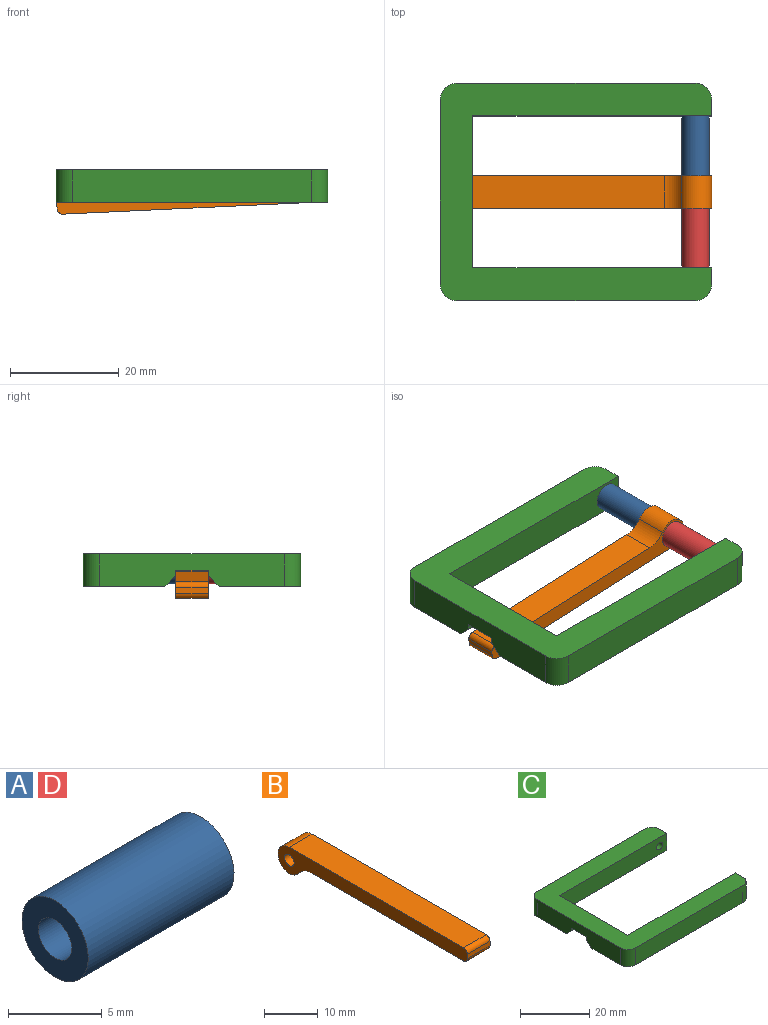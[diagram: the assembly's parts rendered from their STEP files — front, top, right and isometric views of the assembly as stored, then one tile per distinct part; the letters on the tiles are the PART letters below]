
ASSEMBLY  parts=4 mates=4
PART A: 4 faces, bbox 11x5x5 mm
  f0: cylinder r=1.25mm len=11mm, axis (-1,0,0), area 86.4mm2, adj f2,f3
  f1: cylinder r=2.5mm len=11mm, axis (-1,0,0), area 172.8mm2, adj f2,f3
  f2: plane 5x5mm, normal (1,0,0), area 14.7mm2, adj f0,f1
  f3: plane 5x5mm, normal (-1,0,0), area 14.7mm2, adj f0,f1
PART B: 10 faces, bbox 6x50x6 mm
  f0: plane 46x6mm, normal (0,0,1), area 276mm2, adj f4,f6,f7,f8
  f1: plane 6x1mm, normal (0,-1,0), area 6mm2, adj f6,f7,f8,f9
  f2: plane 40.26x6mm, normal (0,0,-1), area 241.5mm2, adj f3,f6,f7,f9
  f3: cylinder r=4mm len=6mm, axis (-1,0,0), area 23.1mm2, adj f2,f4,f6,f7
  f4: cylinder r=3mm len=6mm, axis (-1,0,0), area 73.9mm2, adj f0,f3,f6,f7
  f5: cylinder r=1.25mm len=6mm, axis (-1,0,0), area 47.1mm2, adj f6,f7
  f6: plane 50x6mm, normal (1,0,0), area 157.9mm2, adj f0,f1,f2,f3,f4,f5,f8,f9
  f7: plane 50x6mm, normal (-1,0,0), area 157.9mm2, adj f0,f1,f2,f3,f4,f5,f8,f9
  f8: cylinder r=1mm len=6mm, axis (1,0,0), area 9.4mm2, adj f0,f1,f6,f7
  f9: cylinder r=1mm len=6mm, axis (-1,0,0), area 9.4mm2, adj f1,f2,f6,f7
PART C: 66 faces, bbox 50x40x6 mm
  f0: plane 50x15mm, normal (0,0,-1), area 342.5mm2, adj f1,f2,f3,f4,f5,f6,f12,f21
  f1: plane 28x6mm, normal (1,0,0), area 146mm2, adj f0,f11,f12,f13,f14,f18,f19,f20
  f2: plane 44x6mm, normal (0,1,0), area 261.5mm2, adj f0,f4,f5,f13,f15
  f3: plane 6x3mm, normal (1,0,0), area 18mm2, adj f0,f4,f12,f13
  f4: cylinder r=3mm len=6mm, axis (0,0,-1), area 25.8mm2, adj f0,f2,f3,f13,f15
  f5: cylinder r=3mm len=6mm, axis (0,0,-1), area 28.3mm2, adj f0,f2,f6,f13
  f6: plane 34x6mm, normal (-1,0,0), area 182mm2, adj f0,f5,f7,f13,f14,f18,f19,f20
  f7: cylinder r=3mm len=6mm, axis (0,0,-1), area 28.3mm2, adj f6,f8,f13,f14
  f8: plane 44x6mm, normal (0,-1,0), area 264mm2, adj f7,f9,f13,f14
  f9: cylinder r=3mm len=6mm, axis (0,0,-1), area 28.3mm2, adj f8,f10,f13,f14
  f10: plane 6x3mm, normal (1,0,0), area 18mm2, adj f9,f11,f13,f14
  f11: plane 44x6mm, normal (0,1,0), area 259.1mm2, adj f1,f10,f13,f14,f16
  f12: plane 44x6mm, normal (0,-1,0), area 259.1mm2, adj f0,f1,f3,f13,f15
  f13: plane 50x40mm, normal (0,0,1), area 760.3mm2, adj f1,f2,f3,f4,f5,f6,f7,f8
  f14: plane 50x15mm, normal (0,0,-1), area 350.1mm2, adj f1,f6,f7,f8,f9,f10,f11,f22
  f15: cylinder r=1.25mm len=6mm, axis (0,-1,0), area 46.6mm2, adj f2,f4,f12
  f16: cylinder r=1.25mm len=5mm, axis (0,-1,0), area 39.3mm2, adj f11,f17
  f17: plane 2.5x2.5mm, normal (0,1,0), area 4.9mm2, adj f16
  f18: plane 6x1mm, normal (0,1,0), area 6mm2, adj f1,f6,f20,f22
  f19: plane 6x1mm, normal (0,-1,0), area 6mm2, adj f1,f6,f20,f21
  f20: plane 6x6mm, normal (0,0,-1), area 36mm2, adj f1,f6,f18,f19
  f21: plane 6x2mm, normal (0,-0.71,-0.71), area 17mm2, adj f0,f1,f6,f19
  f22: plane 6x2mm, normal (0,0.71,-0.71), area 17mm2, adj f1,f6,f14,f18
  f23: extruded ~1x0.34mm, area 0.4mm2, adj f0,f24,f30,f31
  f24: extruded ~1x0.34mm, area 0.4mm2, adj f0,f23,f25,f31
  f25: extruded ~1x0.35mm, area 0.4mm2, adj f0,f24,f26,f31
  f26: extruded ~1x0.35mm, area 0.4mm2, adj f0,f25,f27,f31
  f27: extruded ~1x0.34mm, area 0.4mm2, adj f0,f26,f28,f31
  f28: extruded ~1x0.34mm, area 0.4mm2, adj f0,f27,f29,f31
  f29: extruded ~1x0.35mm, area 0.4mm2, adj f0,f28,f30,f31
  f30: extruded ~1x0.36mm, area 0.4mm2, adj f0,f23,f29,f31
  f31: plane 0.95x0.92mm, normal (0,0,-1), area 0.7mm2, adj f23,f24,f25,f26,f27,f28,f29,f30
  f32: extruded ~1x0.34mm, area 0.4mm2, adj f0,f33,f39,f40
  f33: extruded ~1x0.34mm, area 0.4mm2, adj f0,f32,f34,f40
  f34: extruded ~1x0.35mm, area 0.4mm2, adj f0,f33,f35,f40
  f35: extruded ~1x0.35mm, area 0.4mm2, adj f0,f34,f36,f40
  f36: extruded ~1x0.34mm, area 0.4mm2, adj f0,f35,f37,f40
  f37: extruded ~1x0.34mm, area 0.4mm2, adj f0,f36,f38,f40
  f38: extruded ~1x0.35mm, area 0.4mm2, adj f0,f37,f39,f40
  f39: extruded ~1x0.36mm, area 0.4mm2, adj f0,f32,f38,f40
  f40: plane 0.95x0.92mm, normal (0,0,-1), area 0.7mm2, adj f32,f33,f34,f35,f36,f37,f38,f39
  f41: extruded ~1x0.34mm, area 0.4mm2, adj f0,f42,f48,f49
  f42: extruded ~1x0.34mm, area 0.4mm2, adj f0,f41,f43,f49
  f43: extruded ~1x0.35mm, area 0.4mm2, adj f0,f42,f44,f49
  f44: extruded ~1x0.35mm, area 0.4mm2, adj f0,f43,f45,f49
  f45: extruded ~1x0.34mm, area 0.4mm2, adj f0,f44,f46,f49
  f46: extruded ~1x0.34mm, area 0.4mm2, adj f0,f45,f47,f49
  f47: extruded ~1x0.35mm, area 0.4mm2, adj f0,f46,f48,f49
  f48: extruded ~1x0.36mm, area 0.4mm2, adj f0,f41,f47,f49
  f49: plane 0.95x0.92mm, normal (0,0,-1), area 0.7mm2, adj f41,f42,f43,f44,f45,f46,f47,f48
  f50: extruded ~1x0.74mm, area 0.9mm2, adj f0,f51,f64,f65
  f51: extruded ~1x0.44mm, area 0.5mm2, adj f0,f50,f52,f65
  f52: extruded ~1x0.45mm, area 0.5mm2, adj f0,f51,f53,f65
  f53: plane 1x0.68mm, normal (-0.93,-0.37,0), area 0.7mm2, adj f0,f52,f54,f65
  f54: extruded ~1.16x1mm, area 1.2mm2, adj f0,f53,f55,f65
  f55: extruded ~1x0.99mm, area 1mm2, adj f0,f54,f56,f65
  f56: extruded ~1x0.71mm, area 1mm2, adj f0,f55,f57,f65
  f57: extruded ~1.08x1mm, area 1.1mm2, adj f0,f56,f58,f65
  f58: extruded ~1.51x1mm, area 1.6mm2, adj f0,f57,f59,f65
  f59: extruded ~1.32x1mm, area 1.5mm2, adj f0,f58,f60,f65
  f60: extruded ~1.09x1mm, area 1.1mm2, adj f0,f59,f61,f65
  f61: plane 1x0.71mm, normal (-1,0,0), area 0.7mm2, adj f0,f60,f62,f65
  f62: extruded ~1.01x1mm, area 1mm2, adj f0,f61,f63,f65
  f63: extruded ~1.33x1mm, area 1.9mm2, adj f0,f62,f64,f65
  f64: extruded ~1x0.99mm, area 1mm2, adj f0,f50,f63,f65
  f65: plane 4.08x3.02mm, normal (0,0,-1), area 5.5mm2, adj f50,f51,f52,f53,f54,f55,f56,f57
PART D: same geometry as A
PLACE A rot(axis=(0,0,1),90deg) t=(-1.32,-21.35,-12.07)mm
PLACE B rot(axis=(0.71,0.71,0.02),178.1deg) t=(-1.32,-27.35,-12.07)mm
PLACE C t=(1.68,-4.35,-15.07)mm fixed
PLACE D rot(axis=(-0.16,-0.16,0.97),91.5deg) t=(-1.32,-38.35,-12.07)mm
MATE revolute C.f15 <-> A.f1  axis (0,-1,0) through (-1.32,-10.35,-12.07)mm
MATE revolute D.f1 <-> B.f5  axis (0,1,0) through (-1.32,-27.35,-12.07)mm
MATE revolute C.f15 <-> D.f1  axis (0,-1,0) through (-1.32,-38.35,-12.07)mm
MATE planar C.f19 <-> B.f6  axis (0,-1,0) through (-45.32,-21.35,-12.57)mm
